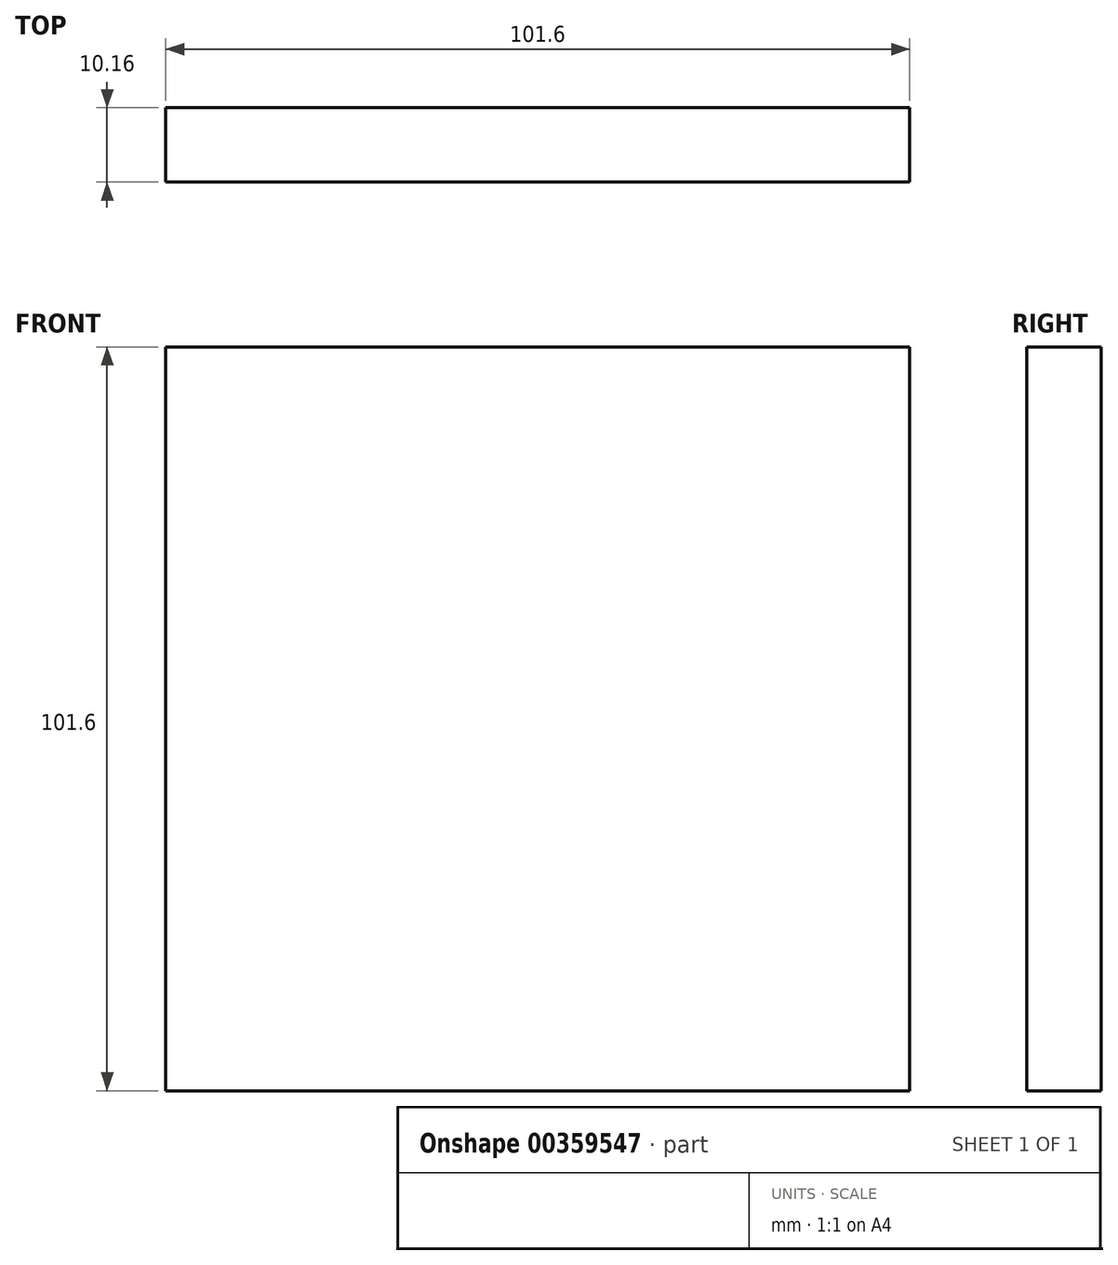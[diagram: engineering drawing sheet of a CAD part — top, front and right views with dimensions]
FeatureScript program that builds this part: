
annotation { "Feature Type Name" : "Feature", "Feature Type Description" : "" }
export const myFeature = defineFeature(function(context is Context, id is Id, definition is map)
    precondition{}
    {
        {
            var Q0;
            Q0=qCreatedBy(makeId("Front.planeOp"),FACE);
            var sketch = newSketch(context, id + "F0", { "sketchPlane" : qUnion([Q0])});
            skLineSegment(sketch, "E0.bottom", {"start": v(50.8, -50.8) * mm, "end": v(-50.8, -50.8) * mm});
            skLineSegment(sketch, "E0.top", {"start": v(50.8, 50.8) * mm, "end": v(-50.8, 50.8) * mm});
            skLineSegment(sketch, "E0.left", {"start": v(50.8, -50.8) * mm, "end": v(50.8, 50.8) * mm});
            skLineSegment(sketch, "E0.right", {"start": v(-50.8, -50.8) * mm, "end": v(-50.8, 50.8) * mm});
            skPoint(sketch, "E0.middle", {"position": v(0, 0) * mm});
            skSolve(sketch);
        }
        {
            var Q0;
            Q0=makeQuery(id+"F0.imprint","IMPRINT",FACE,{"disambiguationData":[TD([[makeQuery(id+"F0.imprint","IMPRINT",EDGE,{"derivedFrom":sQuery(id+"F0.wireOp",EDGE,"E0.bottom")}),-1.0]])]});
            extrude(context, id + "F1", {"entities" : qUnion([Q0]), "depth" : 10.16 * mm});
        }
    });
